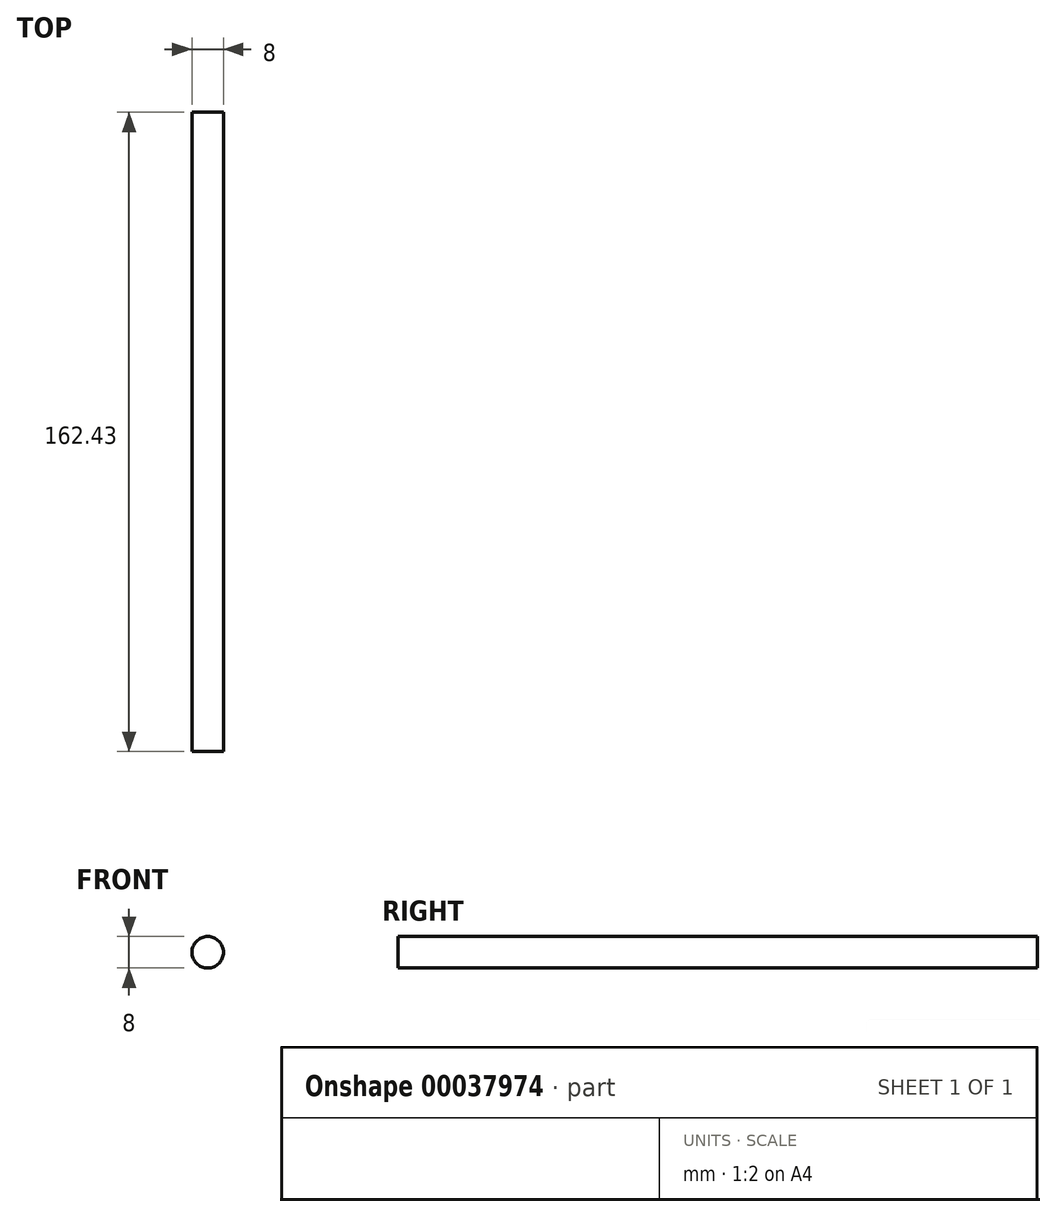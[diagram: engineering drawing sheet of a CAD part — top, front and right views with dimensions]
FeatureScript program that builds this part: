
annotation { "Feature Type Name" : "Feature", "Feature Type Description" : "" }
export const myFeature = defineFeature(function(context is Context, id is Id, definition is map)
    precondition{}
    {
        {
            var Q0;
            Q0=qCreatedBy(makeId("Front.planeOp"),FACE);
            var sketch = newSketch(context, id + "F0", { "sketchPlane" : qUnion([Q0])});
            skCircle(sketch, "E0", {"center": v(0, 0) * mm, "radius": 4 * mm});
            skSolve(sketch);
        }
        {
            var Q0;
            Q0=qSketchRegion(id+"F0",true);
            extrude(context, id + "F1", {"entities" : qUnion([Q0]), "depth" : 162.43 * mm});
        }
    });
